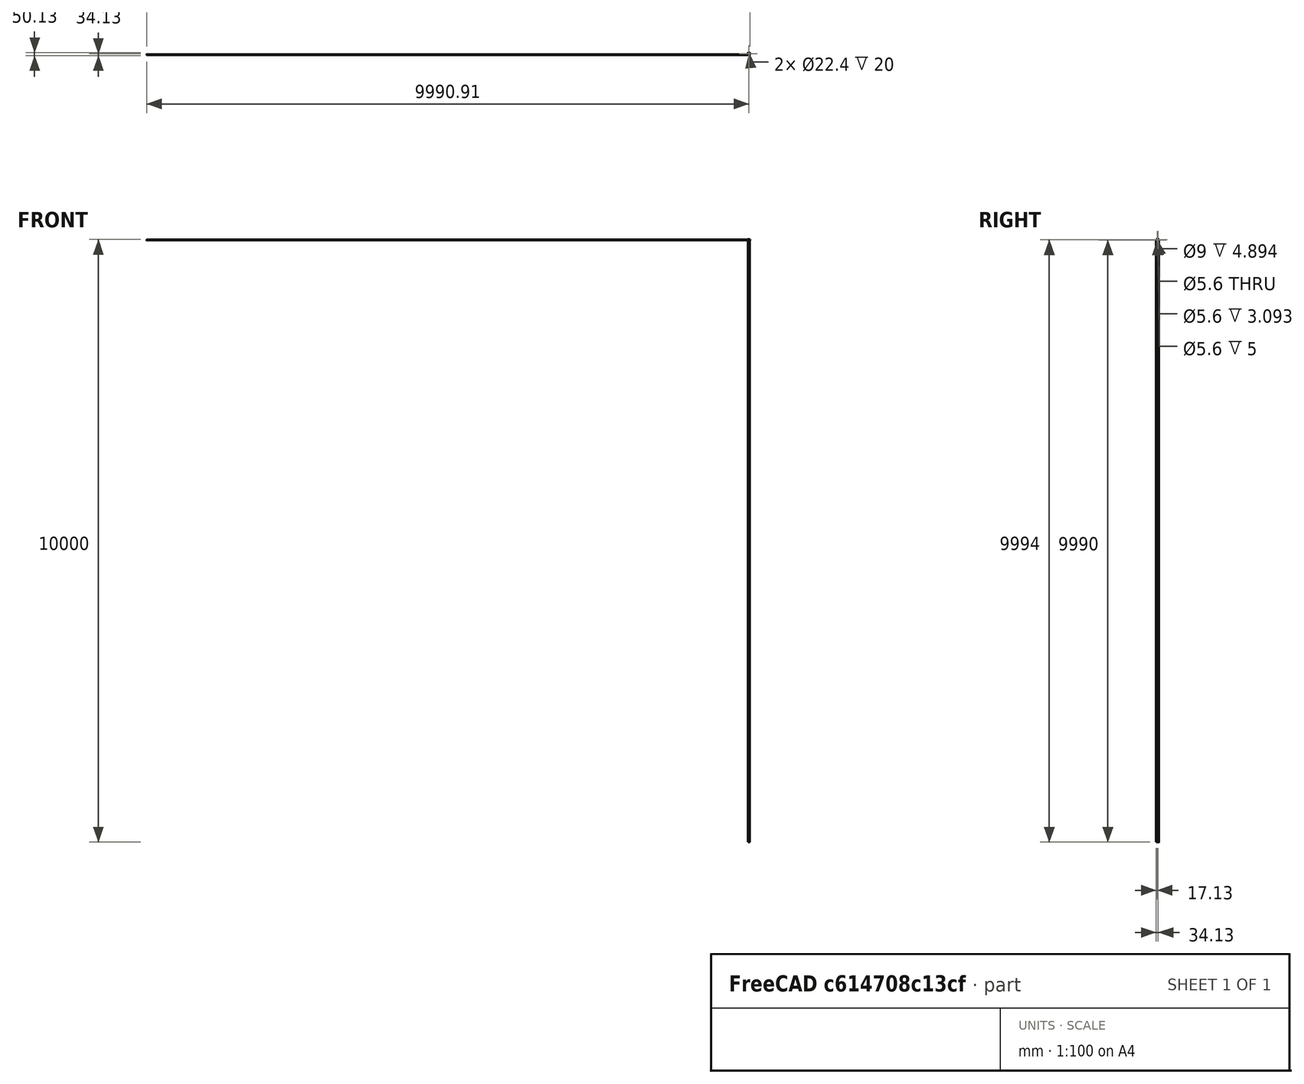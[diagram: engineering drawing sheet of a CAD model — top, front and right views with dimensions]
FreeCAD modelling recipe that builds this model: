
FCSTD DOCUMENT  (FreeCAD 0.16R)
Label: iSpecmount2
License: All rights reserved
LicenseURL: http://en.wikipedia.org/wiki/All_rights_reserved
objects: Sketcher::SketchObject×12, PartDesign::Pocket×9, PartDesign::Fillet×4, PartDesign::Pad×3, Mesh::Feature×1
note: 40 computed .brp shape members not serialized (recipe doc carries the construction recipe); baked Part::Feature solids carry a one-line shape summary decoded from their .brp

FEATURE [Sketcher::SketchObject] Sketch
  sketch-geometry (1):
    g0: Circle CenterX=0 CenterY=0 CenterZ=0 NormalX=0 NormalY=0 NormalZ=1 Radius=16
  constraints (2):
    c: Radius(g0) = 16
    c: Coincident(g0,g-1)
FEATURE [PartDesign::Pad] Pad
  Length = 20
  Length2 = 100
  Sketch = -> Sketch
  Type = 0
FEATURE [Sketcher::SketchObject] Sketch001
  Placement = pos=(0,0,20) rot=(0,0,1;0rad)
  Support = -> Pad [Face3]
  sketch-geometry (1):
    g0: Circle CenterX=0 CenterY=0 CenterZ=0 NormalX=0 NormalY=0 NormalZ=1 Radius=11.2
  constraints (2):
    c: Coincident(g0,g-1)
    c: Radius(g0) = 11.2
FEATURE [PartDesign::Pocket] Pocket
  Length = 5
  Sketch = -> Sketch001
  Type = 1
FEATURE [Sketcher::SketchObject] Sketch002
  ExternalGeometry = -> [Pocket]
  Placement = pos=(0,0,20) rot=(0,0,1;0rad)
  Support = -> Pocket [Face3]
  sketch-geometry (4):
    g0: LineSegment StartX=13 StartY=9.5 StartZ=0 EndX=21 EndY=9.5 EndZ=0
    g1: LineSegment StartX=21 StartY=9.5 StartZ=0 EndX=21 EndY=-9.5 EndZ=0
    g2: LineSegment StartX=21 StartY=-9.5 StartZ=0 EndX=13 EndY=-9.5 EndZ=0
    g3: LineSegment StartX=13 StartY=-9.5 StartZ=0 EndX=13 EndY=9.5 EndZ=0
  constraints (12):
    c: Coincident(g0,g1)
    c: Coincident(g1,g2)
    c: Coincident(g2,g3)
    c: Coincident(g3,g0)
    c: Horizontal(g0)
    c: Horizontal(g2)
    c: Vertical(g1)
    c: Vertical(g3)
    c: Distance(g1) = 19
    c: Symmetric(g0,g2,g-1)
    c: Distance(g0) = 8
    c: DistanceX(g2) = 13
FEATURE [PartDesign::Pad] Pad001
  Length = 12
  Length2 = 100
  Reversed = true
  Sketch = -> Sketch002
  Type = 0
FEATURE [Sketcher::SketchObject] Sketch003
  ExternalGeometry = -> [Pad001]
  Placement = pos=(0,0,20) rot=(0,0,1;0rad)
  Support = -> Pad001 [Face6]
  sketch-geometry (4):
    g0: LineSegment StartX=-9.09342 StartY=-13.1647 StartZ=0 EndX=9.09342 EndY=-13.1647 EndZ=0
    g1: LineSegment StartX=9.09342 StartY=-13.1647 StartZ=0 EndX=9.09342 EndY=-22.1647 EndZ=0
    g2: LineSegment StartX=9.09342 StartY=-22.1647 StartZ=0 EndX=-9.09342 EndY=-22.1647 EndZ=0
    g3: LineSegment StartX=-9.09342 StartY=-22.1647 StartZ=0 EndX=-9.09342 EndY=-13.1647 EndZ=0
  constraints (11):
    c: Coincident(g0,g1)
    c: Coincident(g1,g2)
    c: Coincident(g2,g3)
    c: Coincident(g3,g0)
    c: Horizontal(g0)
    c: Horizontal(g2)
    c: Vertical(g1)
    c: Vertical(g3)
    c: Symmetric(g0,g0,g-2)
    c: PointOnObject(g0,g-3)
    c: Distance(g1) = 9
FEATURE [Sketcher::SketchObject] Sketch005
  Placement = pos=(13,0,0) rot=(0.57735,-0.57735,-0.57735;2.0944rad)
  Support = -> Pad001 [Face5]
  sketch-geometry (7):
    g0: LineSegment StartX=1.2e-11 StartY=9.20799 StartZ=0 EndX=4.15 EndY=11.604 EndZ=0
    g1: LineSegment StartX=4.15 StartY=11.604 StartZ=0 EndX=4.15 EndY=16.396 EndZ=0
    g2: LineSegment StartX=4.15 StartY=16.396 StartZ=0 EndX=0 EndY=18.792 EndZ=0
    g3: LineSegment StartX=0 StartY=18.792 StartZ=0 EndX=-4.15 EndY=16.396 EndZ=0
    g4: LineSegment StartX=-4.15 StartY=16.396 StartZ=0 EndX=-4.15 EndY=11.604 EndZ=0
    g5: LineSegment StartX=-4.15 StartY=11.604 StartZ=0 EndX=1.2e-11 EndY=9.20799 EndZ=0
    g6: Circle [constr] CenterX=0 CenterY=14 CenterZ=0 NormalX=0 NormalY=0 NormalZ=1 Radius=4.79201
  constraints (17):
    c: Coincident(g0,g1)
    c: Coincident(g1,g2)
    c: Coincident(g2,g3)
    c: Coincident(g3,g4)
    c: Coincident(g4,g5)
    c: Coincident(g5,g0)
    c: Equal(g0, g1-g5) x5
    c: PointOnObject(g0,g6)
    c: PointOnObject(g1,g6)
    c: PointOnObject(g2,g6)
    c: PointOnObject(g3,g6)
    c: PointOnObject(g4,g6)
    c: PointOnObject(g5,g6)
    c: Distance(g0,g3) = 8.3
    c: Vertical(g1)
    c: PointOnObject(g6,g-2)
    c: DistanceY(g6) = 14
FEATURE [PartDesign::Pocket] Pocket001
  Length = 6
  Midplane = true
  Reversed = true
  Sketch = -> Sketch005
  Type = 0
FEATURE [Sketcher::SketchObject] Sketch008
  Placement = pos=(21,0,0) rot=(0.57735,0.57735,0.57735;2.0944rad)
  Support = -> Pocket001 [Face15]
  sketch-geometry (1):
    g0: Circle CenterX=0 CenterY=14 CenterZ=0 NormalX=0 NormalY=0 NormalZ=1 Radius=2.8
  constraints (3):
    c: Radius(g0) = 2.8
    c: PointOnObject(g0,g-2)
    c: DistanceY(g0) = 14
FEATURE [PartDesign::Pocket] Pocket002
  Length = 15
  Sketch = -> Sketch008
  Type = 0
FEATURE [PartDesign::Pad] Pad002
  Length = 20
  Length2 = 100
  Reversed = true
  Sketch = -> Sketch003
  Type = 0
FEATURE [Sketcher::SketchObject] Sketch004
  Placement = pos=(9.09342,0,0) rot=(0.57735,0.57735,0.57735;2.0944rad)
  Support = -> Pad002 [Face11]
  sketch-geometry (1):
    g0: Circle CenterX=-17 CenterY=10 CenterZ=0 NormalX=0 NormalY=0 NormalZ=1 Radius=2.8
  constraints (3):
    c: Radius(g0) = 2.8
    c: DistanceY(g0) = 10
    c: DistanceX(g0) = -17
FEATURE [PartDesign::Pocket] Pocket003
  Length = 5
  Sketch = -> Sketch004
  Type = 1
FEATURE [Sketcher::SketchObject] Sketch006
  ExternalGeometry = -> [Pocket003]
  Placement = pos=(9.09342,0,0) rot=(0.57735,0.57735,0.57735;2.0944rad)
  Support = -> Pocket003 [Face11]
  sketch-geometry (1):
    g0: Circle CenterX=-17 CenterY=10 CenterZ=0 NormalX=0 NormalY=0 NormalZ=1 Radius=4.5
  constraints (2):
    c: Radius(g0) = 4.5
    c: Coincident(g-3,g0)
FEATURE [PartDesign::Pocket] Pocket004
  Length = 8
  Midplane = true
  Sketch = -> Sketch006
  Type = 0
FEATURE [Sketcher::SketchObject] Sketch009
  ExternalGeometry = -> [Pocket004]
  Placement = pos=(-9.09342,0,0) rot=(0.57735,-0.57735,-0.57735;2.0944rad)
  Support = -> Pocket004 [Face14]
  sketch-geometry (7):
    g0: LineSegment StartX=17 StartY=5.20799 StartZ=0 EndX=21.15 EndY=7.604 EndZ=0
    g1: LineSegment StartX=21.15 StartY=7.604 StartZ=0 EndX=21.15 EndY=12.396 EndZ=0
    g2: LineSegment StartX=21.15 StartY=12.396 StartZ=0 EndX=17 EndY=14.792 EndZ=0
    g3: LineSegment StartX=17 StartY=14.792 StartZ=0 EndX=12.85 EndY=12.396 EndZ=0
    g4: LineSegment StartX=12.85 StartY=12.396 StartZ=0 EndX=12.85 EndY=7.604 EndZ=0
    g5: LineSegment StartX=12.85 StartY=7.604 StartZ=0 EndX=17 EndY=5.20799 EndZ=0
    g6: Circle [constr] CenterX=17 CenterY=10 CenterZ=0 NormalX=0 NormalY=0 NormalZ=1 Radius=4.79201
  constraints (16):
    c: Coincident(g0,g1)
    c: Coincident(g1,g2)
    c: Coincident(g2,g3)
    c: Coincident(g3,g4)
    c: Coincident(g4,g5)
    c: Coincident(g5,g0)
    c: Equal(g0, g1-g5) x5
    c: PointOnObject(g0,g6)
    c: PointOnObject(g1,g6)
    c: PointOnObject(g2,g6)
    c: PointOnObject(g3,g6)
    c: PointOnObject(g4,g6)
    c: PointOnObject(g5,g6)
    c: Distance(g0,g3) = 8.3
    c: Coincident(g6,g-3)
    c: Vertical(g1)
FEATURE [PartDesign::Pocket] Pocket005
  Length = 5
  Sketch = -> Sketch009
  Type = 0
FEATURE [Sketcher::SketchObject] Sketch007
  Placement = pos=(0,0,20) rot=(0,0,1;0rad)
  Support = -> Pocket005 [Face13]
  sketch-geometry (4):
    g0: LineSegment StartX=-1 StartY=-5.18522 StartZ=0 EndX=1 EndY=-5.18522 EndZ=0
    g1: LineSegment StartX=1 StartY=-5.18522 StartZ=0 EndX=1 EndY=-34.1346 EndZ=0
    g2: LineSegment StartX=1 StartY=-34.1346 StartZ=0 EndX=-1 EndY=-34.1346 EndZ=0
    g3: LineSegment StartX=-1 StartY=-34.1346 StartZ=0 EndX=-1 EndY=-5.18522 EndZ=0
  constraints (10):
    c: Coincident(g0,g1)
    c: Coincident(g1,g2)
    c: Coincident(g2,g3)
    c: Coincident(g3,g0)
    c: Horizontal(g0)
    c: Horizontal(g2)
    c: Vertical(g1)
    c: Vertical(g3)
    c: Symmetric(g0,g0,g-2)
    c: Distance(g2) = 2
FEATURE [PartDesign::Pocket] Pocket006
  Length = 5
  Sketch = -> Sketch007
  Type = 1
FEATURE [Sketcher::SketchObject] Sketch010
  Placement = pos=(21,0,0) rot=(0.57735,0.57735,0.57735;2.0944rad)
  Support = -> Pocket006 [Face38]
  sketch-geometry (1):
    g0: Circle CenterX=0 CenterY=14 CenterZ=0 NormalX=0 NormalY=0 NormalZ=1 Radius=2.8
  constraints (3):
    c: Radius(g0) = 2.8
    c: DistanceY(g0) = 14
    c: PointOnObject(g0,g-2)
FEATURE [PartDesign::Pocket] Pocket007
  Length = 26
  Sketch = -> Sketch010
  Type = 0
FEATURE [Sketcher::SketchObject] Sketch011
  Placement = pos=(13,0,0) rot=(0.57735,-0.57735,-0.57735;2.0944rad)
  Support = -> Pocket007 [Face28]
  sketch-geometry (7):
    g0: LineSegment StartX=4.15 StartY=11.604 StartZ=0 EndX=4.15 EndY=16.396 EndZ=0
    g1: LineSegment StartX=4.15 StartY=16.396 StartZ=0 EndX=0 EndY=18.792 EndZ=0
    g2: LineSegment StartX=0 StartY=18.792 StartZ=0 EndX=-4.15 EndY=16.396 EndZ=0
    g3: LineSegment StartX=-4.15 StartY=16.396 StartZ=0 EndX=-4.15 EndY=11.604 EndZ=0
    g4: LineSegment StartX=-4.15 StartY=11.604 StartZ=0 EndX=0 EndY=9.20799 EndZ=0
    g5: LineSegment StartX=0 StartY=9.20799 StartZ=0 EndX=4.15 EndY=11.604 EndZ=0
    g6: Circle [constr] CenterX=0 CenterY=14 CenterZ=0 NormalX=0 NormalY=0 NormalZ=1 Radius=4.79201
  constraints (17):
    c: Coincident(g0,g1)
    c: Coincident(g1,g2)
    c: Coincident(g2,g3)
    c: Coincident(g3,g4)
    c: Coincident(g4,g5)
    c: Coincident(g5,g0)
    c: Equal(g0, g1-g5) x5
    c: PointOnObject(g0,g6)
    c: PointOnObject(g1,g6)
    c: PointOnObject(g2,g6)
    c: PointOnObject(g3,g6)
    c: PointOnObject(g4,g6)
    c: PointOnObject(g5,g6)
    c: Vertical(g0)
    c: Distance(g0,g1) = 8.3
    c: DistanceY(g6) = 14
    c: PointOnObject(g6,g-2)
FEATURE [PartDesign::Pocket] Pocket008
  Length = 6
  Midplane = true
  Reversed = true
  Sketch = -> Sketch011
  Type = 0
FEATURE [PartDesign::Fillet] Fillet
  Base = -> Pocket008 [Edge122,Edge123]
  Radius = 2
FEATURE [PartDesign::Fillet] Fillet001
  Base = -> Fillet [Edge50,Edge68]
  Radius = 1
FEATURE [PartDesign::Fillet] Fillet002
  Base = -> Fillet001 [Edge23,Edge106,Edge32,Edge98]
  Radius = 1
FEATURE [PartDesign::Fillet] Fillet003
  Base = -> Fillet002 [Edge75]
  Radius = 3
FEATURE [Mesh::Feature] Mesh  label="Fillet003 (Meshed)"
